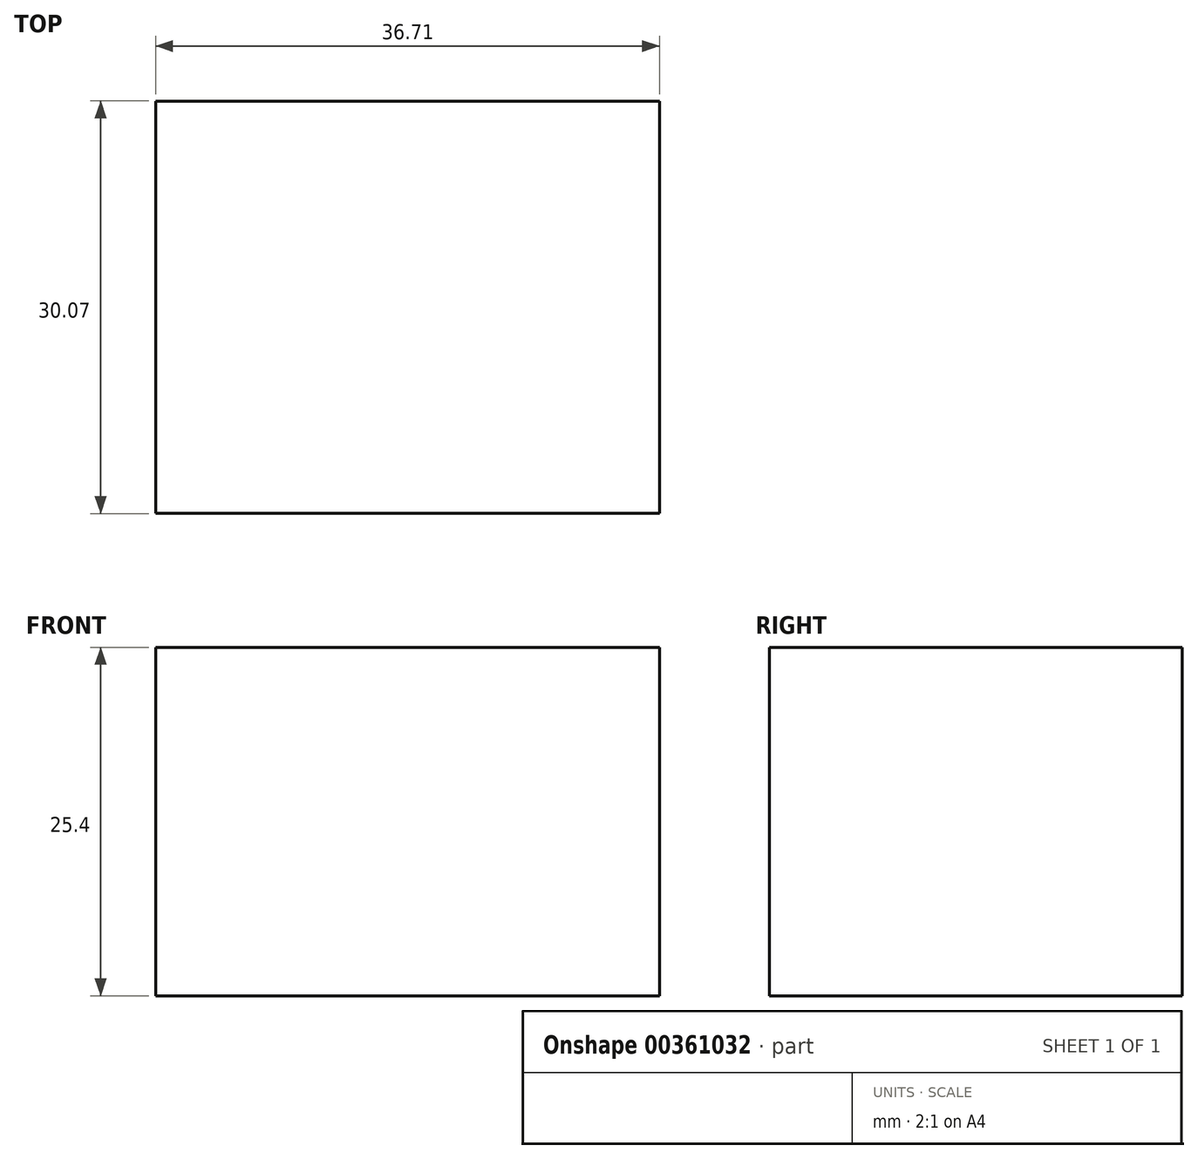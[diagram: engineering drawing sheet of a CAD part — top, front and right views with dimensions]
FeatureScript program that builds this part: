
annotation { "Feature Type Name" : "Feature", "Feature Type Description" : "" }
export const myFeature = defineFeature(function(context is Context, id is Id, definition is map)
    precondition{}
    {
        {
            var Q0;
            Q0=qCreatedBy(makeId("Top.planeOp"),FACE);
            var sketch = newSketch(context, id + "F0", { "sketchPlane" : qUnion([Q0])});
            skLineSegment(sketch, "E0.bottom", {"start": v(-20.35, 13.04) * mm, "end": v(16.36, 13.04) * mm});
            skLineSegment(sketch, "E0.top", {"start": v(-20.35, -17.03) * mm, "end": v(16.36, -17.03) * mm});
            skLineSegment(sketch, "E0.left", {"start": v(-20.35, 13.04) * mm, "end": v(-20.35, -17.03) * mm});
            skLineSegment(sketch, "E0.right", {"start": v(16.36, 13.04) * mm, "end": v(16.36, -17.03) * mm});
            skSolve(sketch);
        }
        {
            var Q0;
            Q0 = qSketchRegion(id + "F0", true);
            extrude(context, id + "F1", {"entities" : qUnion([Q0]), "depth" : 25.4 * mm});
        }
    });
